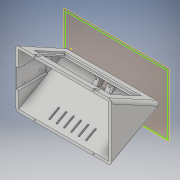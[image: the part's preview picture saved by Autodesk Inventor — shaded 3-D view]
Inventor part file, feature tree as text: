
AUTODESK INVENTOR PART (.ipt)
format: ipt  version: 2018 (Build 220112000, 112)  size: 599,040 bytes
history: native  units: in
note: dims shown in document units (in); Inventor stores cm internally (conversion verified against a paired STEP export)
features: extrude x21, sketch x20, fillet x11, plane x9, split x4, shell x1, chamfer x1
ambient origin geometry x8: Origin, YZ Plane, XZ Plane, XY Plane, X Axis, Y Axis, Z Axis, Center Point
bodies: Solid1 (feature_tree)
feature tree (67):
  extrude  "Extrusion1"  Depth=4.0in
  shell  "Shell1"  Thickness=7.6772in
  extrude  "Extrusion8"  Depth=0.25in
  fillet  "Fillet3"  Radius=0.25in
  sketch  "Sketch10"  dims[d54=0.25in d55=0.25in]
  extrude  "Extrusion10"  Depth=0.25in
  extrude  "Extrusion11"  Depth=0.25in
  fillet  "Fillet14"  Radius=1.0in
  extrude  "Extrusion12"  Depth=0.125in
  plane  "Work Plane2"
  extrude  "Extrusion13"  Depth=0.125in
  plane  "Work Plane4"
  extrude  "Extrusion26"  Depth=0.125in
  extrude  "Extrusion27"  TaperAngle=0.0deg  [1 undecoded]
  fillet  "Fillet15"  [1 undecoded]
  plane  "Work Plane6"
  extrude  "Extrusion28"  Depth=0.1181in
  plane  "Work Plane7"
  extrude  "Extrusion29"  Depth=0.1181in
  extrude  "Extrusion30"  Depth=10.0in TaperAngle=0.0deg
  extrude  "Extrusion31"  Depth=10.0in TaperAngle=0.0deg
  extrude  "Extrusion32"  [1 undecoded]
  fillet  "Fillet16"  Radius=0.2953in
  fillet  "Fillet18"  Radius=0.2953in
  fillet  "Fillet19"  Radius=0.2953in
  extrude  "Extrusion33"  Depth=0.4in TaperAngle=0.0deg
  plane  "Work Plane8"
  split  "Split1"
  plane  "Work Plane9"
  split  "Split2"
  plane  "Work Plane10"
  plane  "Work Plane11"
  split  "Split3"
  split  "Split4"
  extrude  "Extrusion34"  Depth=0.1969in
  extrude  "Extrusion35"  Depth=0.6496in
  fillet  "Fillet21"  Radius=5.0in
  extrude  "Extrusion36"  Depth=0.5in
  chamfer  "Chamfer2"  Distance=0.125in
  fillet  "Fillet23"  Radius=0.125in
  fillet  "Fillet25"  Radius=0.125in
  fillet  "Fillet26"  Radius=0.25in
  extrude  "Extrusion38"  Depth=0.25in
  fillet  "Fillet27"  Radius=0.5in
  extrude  "Extrusion39"  Depth=0.5in
  extrude  "Extrusion40"  Depth=0.5in
  extrude  "Extrusion41"  Depth=0.5in
  plane  "Work Plane12"
  sketch  "Sketch45"  dims[d164=0.125in d165=0.125in d166=0.125in d167=0.125in d168=0.25in d169=0.25in d170=0.5in d171=0.5in d172=0.5in d173=0.5in d174=0.5in d175=0.0in d176=0.0625in d181=90.0deg d182=0.125in d183=0.5in d184=0.5in d185=4.7in d186=0.0in d187=90.0deg d188=4.7in d189=0.0in d190=4.0in d191=0.0in d192=0.242in d193=0.0in d196=0.1181in d197=0.1181in d198=0.1575in d199=0.0in d200=0.0625in d203=0.0394in d204=0.0394in d206=0.6in d207=0.0in d208=-0.4in d209=-3.0in d210=1.136in d211=0.2568in d212=0.2568in d213=0.256in d214=0.2579in d215=-3.0in d216=-3.0in d217=0.1969in d218=2.3622in d219=1.5748in d220=0.0in d221=0.1969in d222=0.0in d223=0.2657in d224=0.6102in d229=0.0787in d230=0.0787in d231=0.0787in d232=0.0787in d233=0.0394in d234=0.0in d236=0.125in d237=0.0394in d238=0.0394in d239=0.0394in d240=0.1969in d241=0.0in d242=0.1181in d243=0.125in d244=45.0deg d245=0.9646in d246=1.3583in d254=0.3937in d256=0.125in d257=0.1575in d258=0.1575in d259=0.1575in d260=0.1969in d261=0.1969in d262=0.1969in d263=0.1969in d264=0.0787in d265=0.0in d266=0.0787in d267=2.5in d268=6.0in d269=0.25in d270=0.0in d271=0.25in d272=0.25in d273=0.25in d274=0.25in d275=0.125in d276=0.0in d277=0.1181in d278=0.1181in d279=0.1181in d280=0.1181in d281=0.125in d282=0.0in d283=-4.5in]
  sketch  "Sketch1"  dims[d0=4.0in d1=4.4094in d2=7.6772in d3=0.0in]
  sketch  "Sketch9"  dims[d4=0.25in d52=0.25in d53=0.25in]
  sketch  "Sketch11"  dims[d56=0.25in d57=0.25in d58=1.0in d59=0.0in]
  sketch  "Sketch12"  dims[d60=0.125in d61=0.125in]
  sketch  "Sketch13"  dims[d62=0.125in d63=0.125in]
  sketch  "Sketch26"  dims[d64=0.125in d65=1.2894in]
  sketch  "Sketch27"  dims[d66=5.0in d67=0.0in d68=0.0in]
  sketch  "Sketch31"  dims[d69=0.1181in d71=0.1181in]
  sketch  "Sketch32"  dims[d72=0.1181in d76=0.1181in]
  sketch  "Sketch33"  dims[d81=1.0in d82=0.0in d85=10.0in d86=0.0in]
  sketch  "Sketch35"  dims[d88=0.315in d89=10.0in d90=0.0in]
  sketch  "Sketch36"  dims[d99=0.2756in d100=-0.5in d101=0.2953in d102=0.2953in d103=0.2953in]
  sketch  "Sketch37"  dims[d104=0.2953in d105=0.4in d106=0.0in]
  sketch  "Sketch39"  dims[d154=90.0deg d155=0.1969in]
  sketch  "Sketch41"  dims[d156=0.5157in d157=0.6496in d158=5.0in d159=0.0in]
  sketch  "Sketch42"  dims[d160=1.0in d161=0.5in]
  sketch  "Sketch43"  dims[d162=0.125in]
  sketch  "Sketch44"  dims[d163=0.125in]
note: 3 required parameter values undecoded (feature->parameter linkage not recoverable at this tier; creation-order binding heuristic only, values carry confidence <= 0.55)
